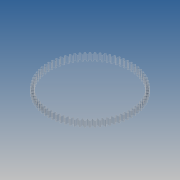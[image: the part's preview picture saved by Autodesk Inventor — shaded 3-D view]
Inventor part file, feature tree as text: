
AUTODESK INVENTOR PART (.ipt)
format: ipt  version: 2017 (Build 210142000, 142)  size: 439,808 bytes
history: native  units: mm (DEFAULTED — no unit token found)
features: plane x3, other x3, sketch x2, extrude x1
ambient origin geometry x8: Origin, YZ Plane, XZ Plane, XY Plane, X Axis, Y Axis, Z Axis, Center Point
bodies: Solid1 (feature_tree)
feature tree (9):
  extrude  "Extrusion1"  Depth=8.0mm TaperAngle=0.0deg
  plane  "Work Plane2"
  plane  "Work Plane8"
  plane  "Work Plane9"
  other  "Engranaje recto"
  sketch  "Sketch1"  dims[d0=111.0mm d1=8.0mm d2=0.0mm]
  sketch  "Sketch2"  dims[d3=108.0mm d4=10.0mm d5=0.0mm d16=67.5mm d17=0.0mm d34=0.436332mm d39=0.0mm d41=0.0mm d43=67.5mm d46=67.5mm d47=0.0mm d48=0.0mm]
  other  "Srf1"
  other  "Diámetro de separación"
